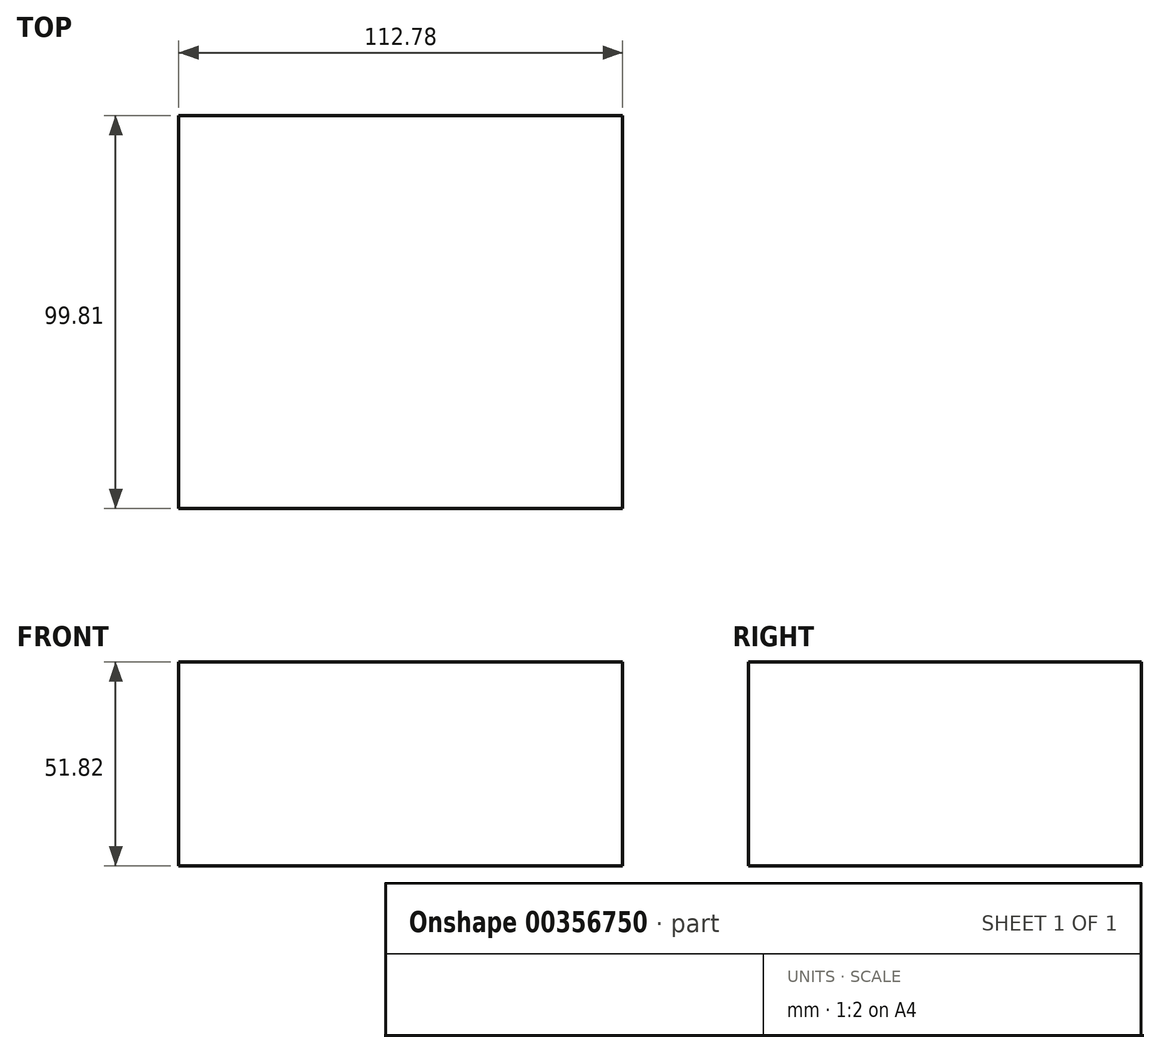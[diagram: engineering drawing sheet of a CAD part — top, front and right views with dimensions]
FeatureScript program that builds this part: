
annotation { "Feature Type Name" : "Feature", "Feature Type Description" : "" }
export const myFeature = defineFeature(function(context is Context, id is Id, definition is map)
    precondition{}
    {
        {
            var Q0;
            Q0=qCreatedBy(makeId("Top.planeOp"),FACE);
            var sketch = newSketch(context, id + "F0", { "sketchPlane" : qUnion([Q0])});
            skLineSegment(sketch, "E0.bottom", {"start": v(-69.65, -49.9) * mm, "end": v(43.13, -49.9) * mm});
            skLineSegment(sketch, "E0.top", {"start": v(-69.65, 49.9) * mm, "end": v(43.13, 49.9) * mm});
            skLineSegment(sketch, "E0.left", {"start": v(-69.65, -49.9) * mm, "end": v(-69.65, 49.9) * mm});
            skLineSegment(sketch, "E0.right", {"start": v(43.13, -49.9) * mm, "end": v(43.13, 49.9) * mm});
            skSolve(sketch);
        }
        {
            var Q0;
            Q0 = qSketchRegion(id + "F0", true);
            extrude(context, id + "F1", {"entities" : qUnion([Q0]), "depth" : 51.82 * mm});
        }
    });
